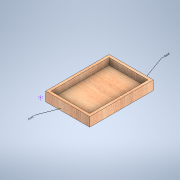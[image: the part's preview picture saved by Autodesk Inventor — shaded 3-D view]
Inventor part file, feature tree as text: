
AUTODESK INVENTOR PART (.ipt)
format: ipt  version: 2020 (Build 240168000, 168)  size: 122,368 bytes
history: native  units: in
note: dims shown in document units (in); Inventor stores cm internally (conversion verified against a paired STEP export)
features: other x3, sketch x2, extrude x1, shell x1
ambient origin geometry x8: Origin, YZ Plane, XZ Plane, XY Plane, X Axis, Y Axis, Z Axis, Center Point
bodies: Solid1 (feature_tree)
feature tree (7):
  other  "Annotations"
  extrude  "Extrusion1"  Depth=14.1732in
  shell  "Shell1"  Thickness=2.0472in
  sketch  "3D Sketch5"
  sketch  "Sketch1"  dims[d0=9.8425in d1=14.1732in d2=2.0472in d3=0.0in d4=0.5906in d5=0.1354in d6=0.0742in d7=0.0893in d8=0.1577in]
  other  "Leader Text 1"
  other  "Leader Text 2"
